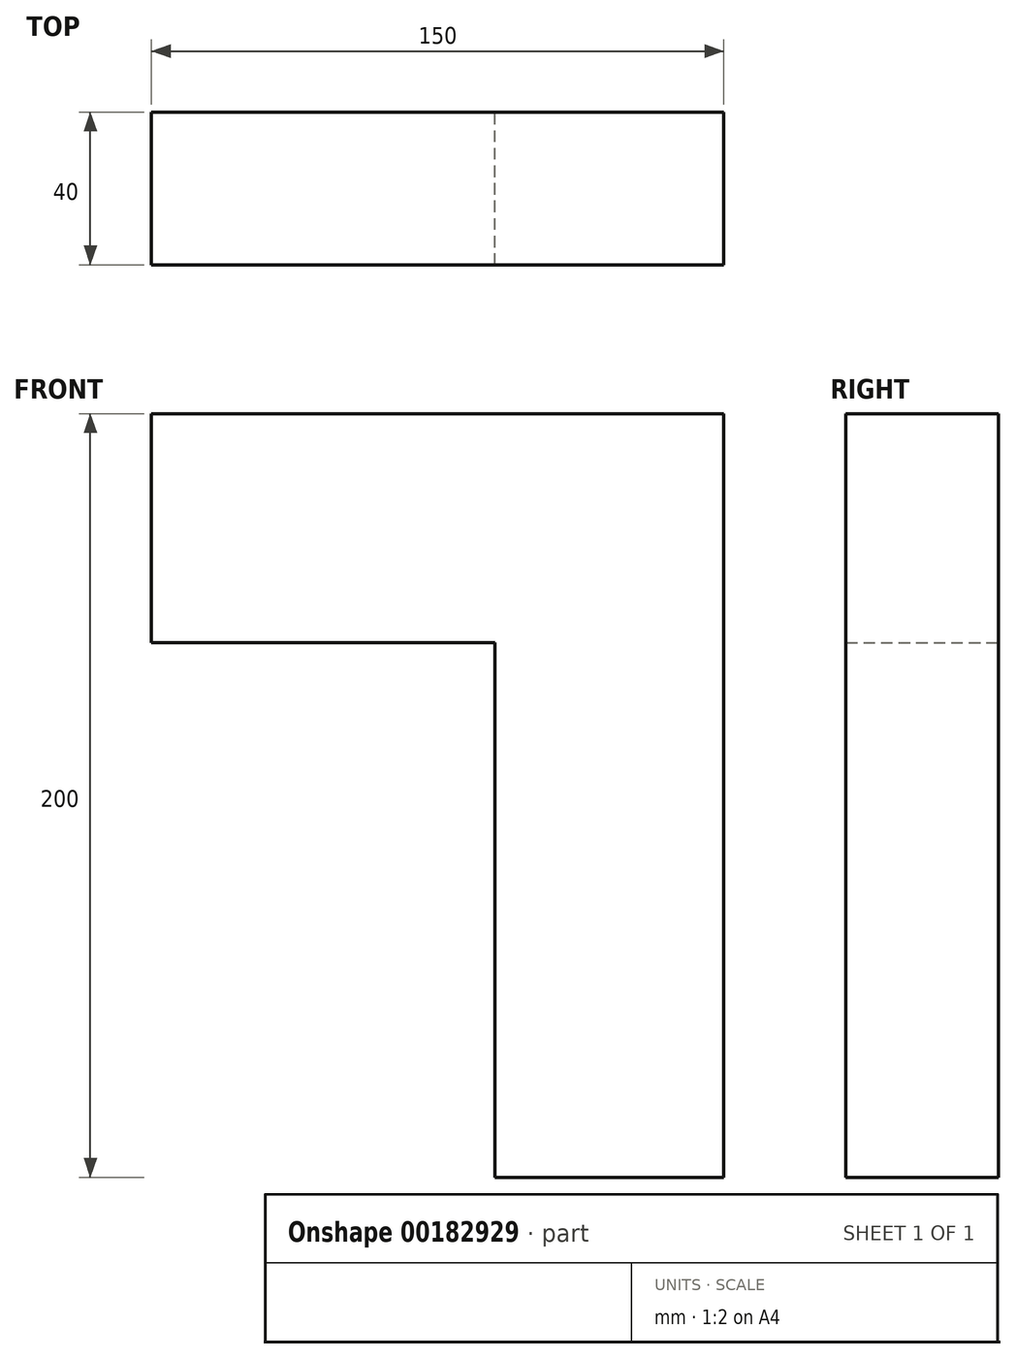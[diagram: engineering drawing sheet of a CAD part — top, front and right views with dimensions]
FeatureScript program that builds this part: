
annotation { "Feature Type Name" : "Feature", "Feature Type Description" : "" }
export const myFeature = defineFeature(function(context is Context, id is Id, definition is map)
    precondition{}
    {
        {
            var Q0;
            Q0=qCreatedBy(makeId("Front.planeOp"),FACE);
            var sketch = newSketch(context, id + "F0", { "sketchPlane" : qUnion([Q0])});
            skLineSegment(sketch, "E0", {"start": v(0, 0) * mm, "end": v(0, 200) * mm});
            skLineSegment(sketch, "E1", {"start": v(-150, 200) * mm, "end": v(-150, 140) * mm});
            skLineSegment(sketch, "E2", {"start": v(-150, 140) * mm, "end": v(-60, 140) * mm});
            skLineSegment(sketch, "E3", {"start": v(-60, 140) * mm, "end": v(-60, 0) * mm});
            skLineSegment(sketch, "E4", {"start": v(-60, 0) * mm, "end": v(0, 0) * mm});
            skLineSegment(sketch, "E5", {"start": v(0, 200) * mm, "end": v(-150, 200) * mm});
            skSolve(sketch);
        }
        {
            var Q0;
            Q0=qSketchRegion(id+"F0",true);
            extrude(context, id + "F1", {"entities" : qUnion([Q0]), "depth" : 40 * mm});
        }
    });
